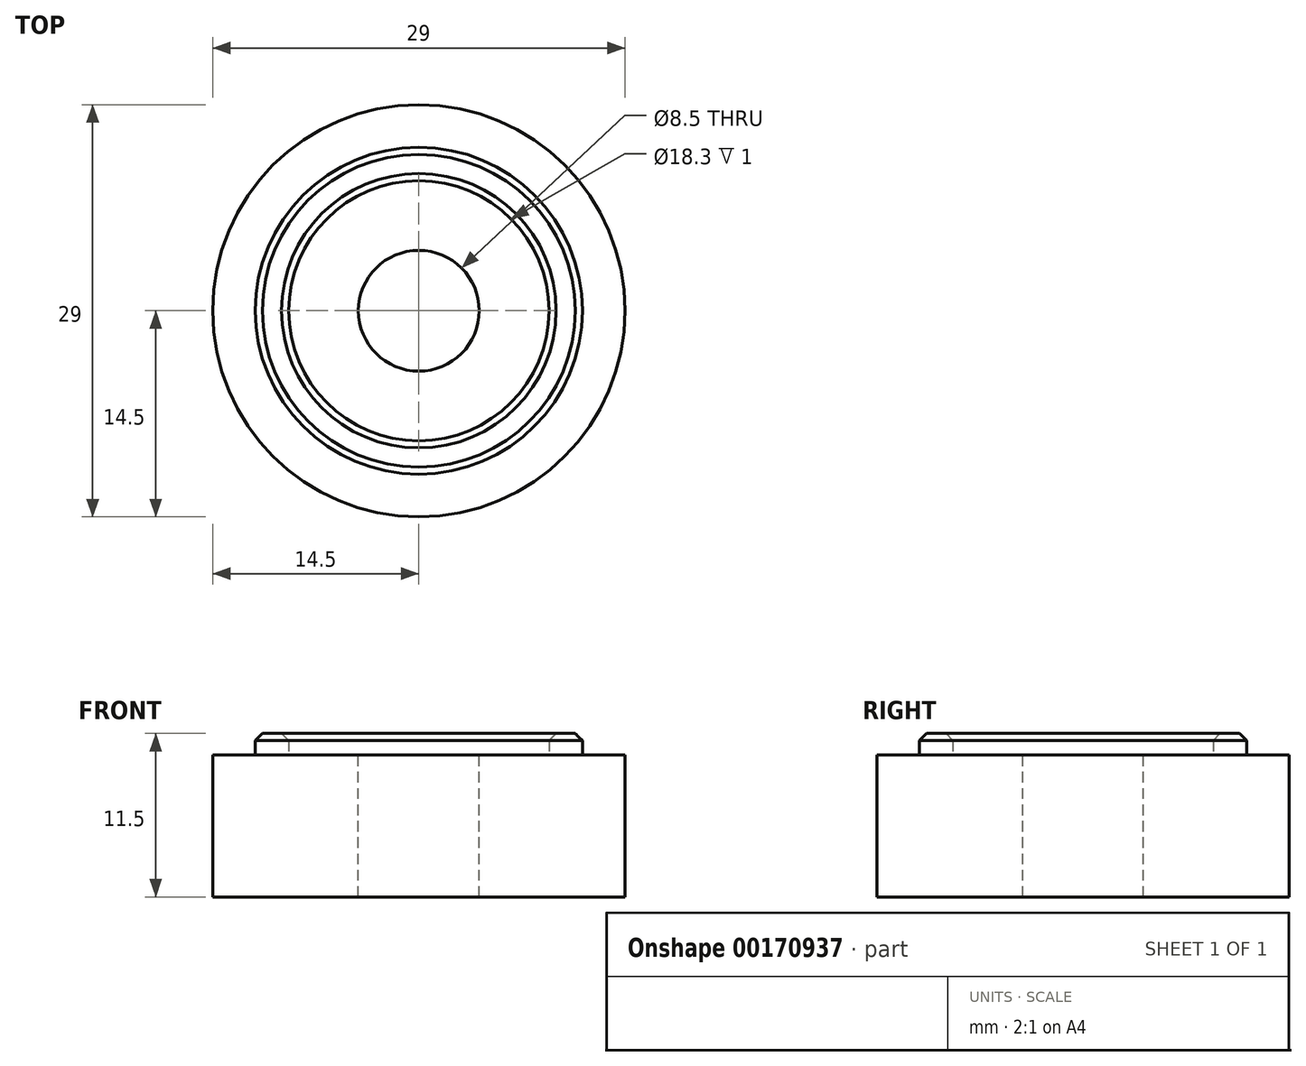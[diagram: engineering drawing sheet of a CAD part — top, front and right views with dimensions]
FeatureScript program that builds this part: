
annotation { "Feature Type Name" : "Feature", "Feature Type Description" : "" }
export const myFeature = defineFeature(function(context is Context, id is Id, definition is map)
    precondition{}
    {
        {
            var Q0;
            Q0=qCreatedBy(makeId("Top.planeOp"),FACE);
            var sketch = newSketch(context, id + "F0", { "sketchPlane" : qUnion([Q0])});
            skCircle(sketch, "E0", {"center": v(0, 0) * mm, "radius": 14.5 * mm});
            skCircle(sketch, "E1", {"center": v(0, 0) * mm, "radius": 4.25 * mm});
            skCircle(sketch, "E2", {"center": v(0, 0) * mm, "radius": 11.65 * mm, "construction": true});
            skLineSegment(sketch, "E3", {"start": v(-23.2, 0) * mm, "end": v(37.67, 0) * mm, "construction": true});
            skPoint(sketch, "E4", {"position": v(11.65, 0) * mm});
            skPoint(sketch, "E5", {"position": v(14.5, 0) * mm});
            skCircle(sketch, "E6", {"center": v(0, 0) * mm, "radius": 9 * mm, "construction": true});
            skCircle(sketch, "E7.0", {"center": v(0, 0) * mm, "radius": 9.15 * mm});
            skCircle(sketch, "E8.0", {"center": v(0, 0) * mm, "radius": 11.5 * mm});
            skSolve(sketch);
        }
        {
            var Q0;
            Q0=makeQuery(id+"F0.imprint","IMPRINT",FACE,{"disambiguationData":[TD([[makeQuery(id+"F0.imprint","IMPRINT",EDGE,{"derivedFrom":sQuery(id+"F0.wireOp",EDGE,"E0")}),1.0]])]});
            var Q1;
            Q1=makeQuery(id+"F0.imprint","IMPRINT",FACE,{"disambiguationData":[TD([[makeQuery(id+"F0.imprint","IMPRINT",EDGE,{"derivedFrom":sQuery(id+"F0.wireOp",EDGE,"E7.0")}),-1.0]])]});
            var Q2;
            Q2=makeQuery(id+"F0.imprint","IMPRINT",FACE,{"disambiguationData":[TD([[makeQuery(id+"F0.imprint","IMPRINT",EDGE,{"derivedFrom":sQuery(id+"F0.wireOp",EDGE,"E1")}),-1.0]])]});
            extrude(context, id + "F1", {"entities" : qUnion([Q0, Q1, Q2]), "oppositeDirection" : true, "depth" : 10 * mm});
        }
        {
            var Q0;
            Q0=makeQuery(id+"F0.imprint","IMPRINT",FACE,{"disambiguationData":[TD([[makeQuery(id+"F0.imprint","IMPRINT",EDGE,{"derivedFrom":sQuery(id+"F0.wireOp",EDGE,"E7.0")}),-1.0]])]});
            extrude(context, id + "F2", {"entities" : qUnion([Q0]), "operationType" : NewBodyOperationType.ADD, "depth" : 1.5 * mm});
        }
        {
            var Q0;
            Q0=makeQuery(id+"F2.opExtrude","CAP_EDGE",EDGE,{"disambiguationData":[OSD([sQuery(id+"F0.wireOp",EDGE,"E8.0")])],"isStart":false});
            var Q1;
            Q1=makeQuery(id+"F2.opExtrude","CAP_EDGE",EDGE,{"disambiguationData":[OSD([sQuery(id+"F0.wireOp",EDGE,"E7.0")])],"isStart":false});
            chamfer(context, id + "F3", {"entities" : qUnion([Q0, Q1]), "width" : .5 * mm, "tangentPropagation" : true});
        }
    });
